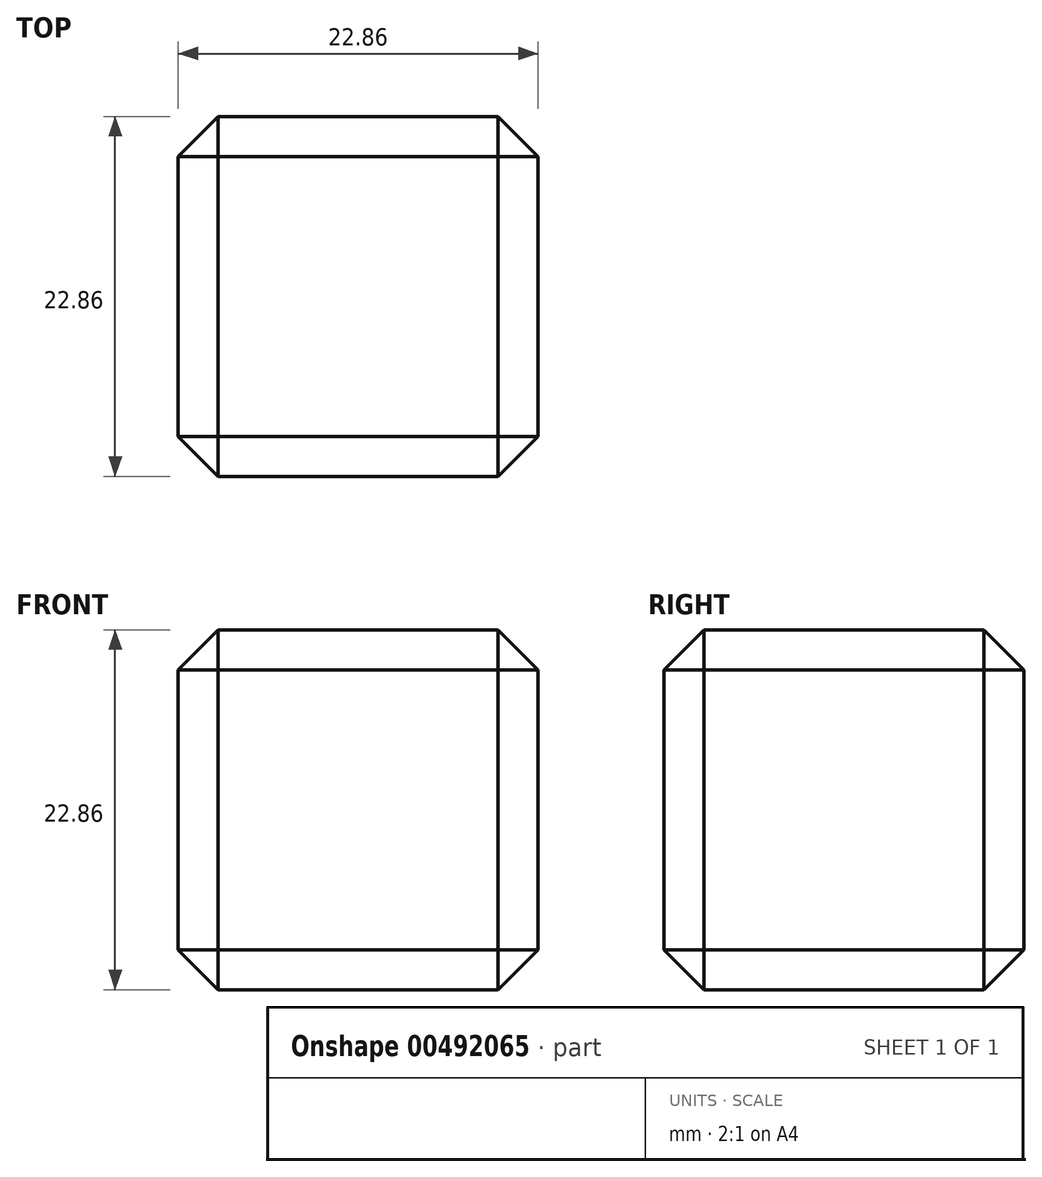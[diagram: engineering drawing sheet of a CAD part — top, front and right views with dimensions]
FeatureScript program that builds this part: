
annotation { "Feature Type Name" : "Feature", "Feature Type Description" : "" }
export const myFeature = defineFeature(function(context is Context, id is Id, definition is map)
    precondition{}
    {
        {
            var Q0;
            Q0=qCreatedBy(makeId("Top.planeOp"),FACE);
            var sketch = newSketch(context, id + "F0", { "sketchPlane" : qUnion([Q0])});
            skLineSegment(sketch, "E0.bottom", {"start": v(11.43, -11.43) * mm, "end": v(-11.43, -11.43) * mm});
            skLineSegment(sketch, "E0.top", {"start": v(11.43, 11.43) * mm, "end": v(-11.43, 11.43) * mm});
            skLineSegment(sketch, "E0.left", {"start": v(11.43, -11.43) * mm, "end": v(11.43, 11.43) * mm});
            skLineSegment(sketch, "E0.right", {"start": v(-11.43, -11.43) * mm, "end": v(-11.43, 11.43) * mm});
            skPoint(sketch, "E0.middle", {"position": v(0, 0) * mm});
            skSolve(sketch);
        }
        {
            var Q0;
            Q0 = qSketchRegion(id + "F0", true);
            extrude(context, id + "F1", {"entities" : qUnion([Q0]), "depth" : 22.86 * mm, "offsetDistance" : 25 * mm});
        }
        {
            var Q0;
            Q0=makeQuery(id+"F1.opExtrude","SWEPT_EDGE",EDGE,{"disambiguationData":[OSD([sQuery(id+"F0.wireOp",EDGE,"E0.bottom"),sQuery(id+"F0.wireOp",EDGE,"E0.left")])]});
            var Q1;
            Q1=makeQuery(id+"F1.opExtrude","SWEPT_EDGE",EDGE,{"disambiguationData":[OSD([sQuery(id+"F0.wireOp",EDGE,"E0.bottom"),sQuery(id+"F0.wireOp",EDGE,"E0.right")])]});
            var Q2;
            Q2=makeQuery(id+"F1.opExtrude","SWEPT_EDGE",EDGE,{"disambiguationData":[OSD([sQuery(id+"F0.wireOp",EDGE,"E0.top"),sQuery(id+"F0.wireOp",EDGE,"E0.left")])]});
            var Q3;
            Q3=makeQuery(id+"F1.opExtrude","CAP_EDGE",EDGE,{"disambiguationData":[OSD([sQuery(id+"F0.wireOp",EDGE,"E0.bottom")])],"isStart":false});
            var Q4;
            Q4=makeQuery(id+"F1.opExtrude","CAP_EDGE",EDGE,{"disambiguationData":[OSD([sQuery(id+"F0.wireOp",EDGE,"E0.top")])],"isStart":false});
            var Q5;
            Q5=makeQuery(id+"F1.opExtrude","CAP_EDGE",EDGE,{"disambiguationData":[OSD([sQuery(id+"F0.wireOp",EDGE,"E0.left")])],"isStart":true});
            var Q6;
            Q6=makeQuery(id+"F1.opExtrude","CAP_EDGE",EDGE,{"disambiguationData":[OSD([sQuery(id+"F0.wireOp",EDGE,"E0.left")])],"isStart":false});
            var Q7;
            Q7=makeQuery(id+"F1.opExtrude","CAP_EDGE",EDGE,{"disambiguationData":[OSD([sQuery(id+"F0.wireOp",EDGE,"E0.right")])],"isStart":false});
            var Q8;
            Q8=makeQuery(id+"F1.opExtrude","SWEPT_EDGE",EDGE,{"disambiguationData":[OSD([sQuery(id+"F0.wireOp",EDGE,"E0.top"),sQuery(id+"F0.wireOp",EDGE,"E0.right")])]});
            var Q9;
            Q9=makeQuery(id+"F1.opExtrude","CAP_EDGE",EDGE,{"disambiguationData":[OSD([sQuery(id+"F0.wireOp",EDGE,"E0.bottom")])],"isStart":true});
            var Q10;
            Q10=makeQuery(id+"F1.opExtrude","CAP_EDGE",EDGE,{"disambiguationData":[OSD([sQuery(id+"F0.wireOp",EDGE,"E0.top")])],"isStart":true});
            var Q11;
            Q11=makeQuery(id+"F1.opExtrude","CAP_EDGE",EDGE,{"disambiguationData":[OSD([sQuery(id+"F0.wireOp",EDGE,"E0.right")])],"isStart":true});
            chamfer(context, id + "F2", {"entities" : qUnion([Q0, Q1, Q2, Q3, Q4, Q5, Q6, Q7, Q8, Q9, Q10, Q11]), "width" : 2.54 * mm, "tangentPropagation" : true});
        }
    });
